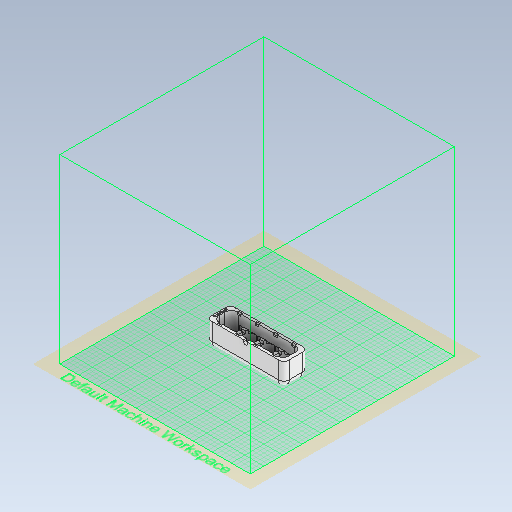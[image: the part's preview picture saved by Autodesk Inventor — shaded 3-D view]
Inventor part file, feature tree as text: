
AUTODESK INVENTOR PART (.ipt)
format: ipt  version: 2021 (Build 250183000, 183)  size: 2,360,832 bytes
history: native  units: in
note: dims shown in document units (in); Inventor stores cm internally (conversion verified against a paired STEP export)
features: extrude x9, other x9, fillet x3
ambient origin geometry x8: Origin, YZ Plane, XZ Plane, XY Plane, X Axis, Y Axis, Z Axis, Center Point
bodies: Body1 (feature_tree)
feature tree (21):
  extrude  "Base"  Depth=6.6929in
  other  "Top Indent Sketch"
  extrude  "Top"  Depth=2.0472in
  extrude  "Walls"  Depth=1.9685in TaperAngle=0.0deg
  fillet  "Outer"  Radius=1.0236in
  extrude  "Outer Wire"  Depth=1.0236in
  extrude  "Wall Holes"  Depth=1.0236in
  extrude  "Text"  Depth=1.0236in
  extrude  "Inner Sketch"  Depth=1.5748in
  fillet  "Inner Fillet"  Radius=1.5748in
  extrude  "Top Indent"  Depth=1.5748in
  other  "Wire Hole Plane"
  extrude  "Wire Hole"  Depth=0.7087in TaperAngle=0.0deg
  fillet  "Fillet10"  Radius=0.315in
  other  "Base Sketch"
  other  "Walls Sketch"
  other  "Outer Wire Sketch"
  other  "Wall Holes Sketch"
  other  "Text Sketch"
  other  "Inner Support Sketch"
  other  "Wire Hole Sketch"
